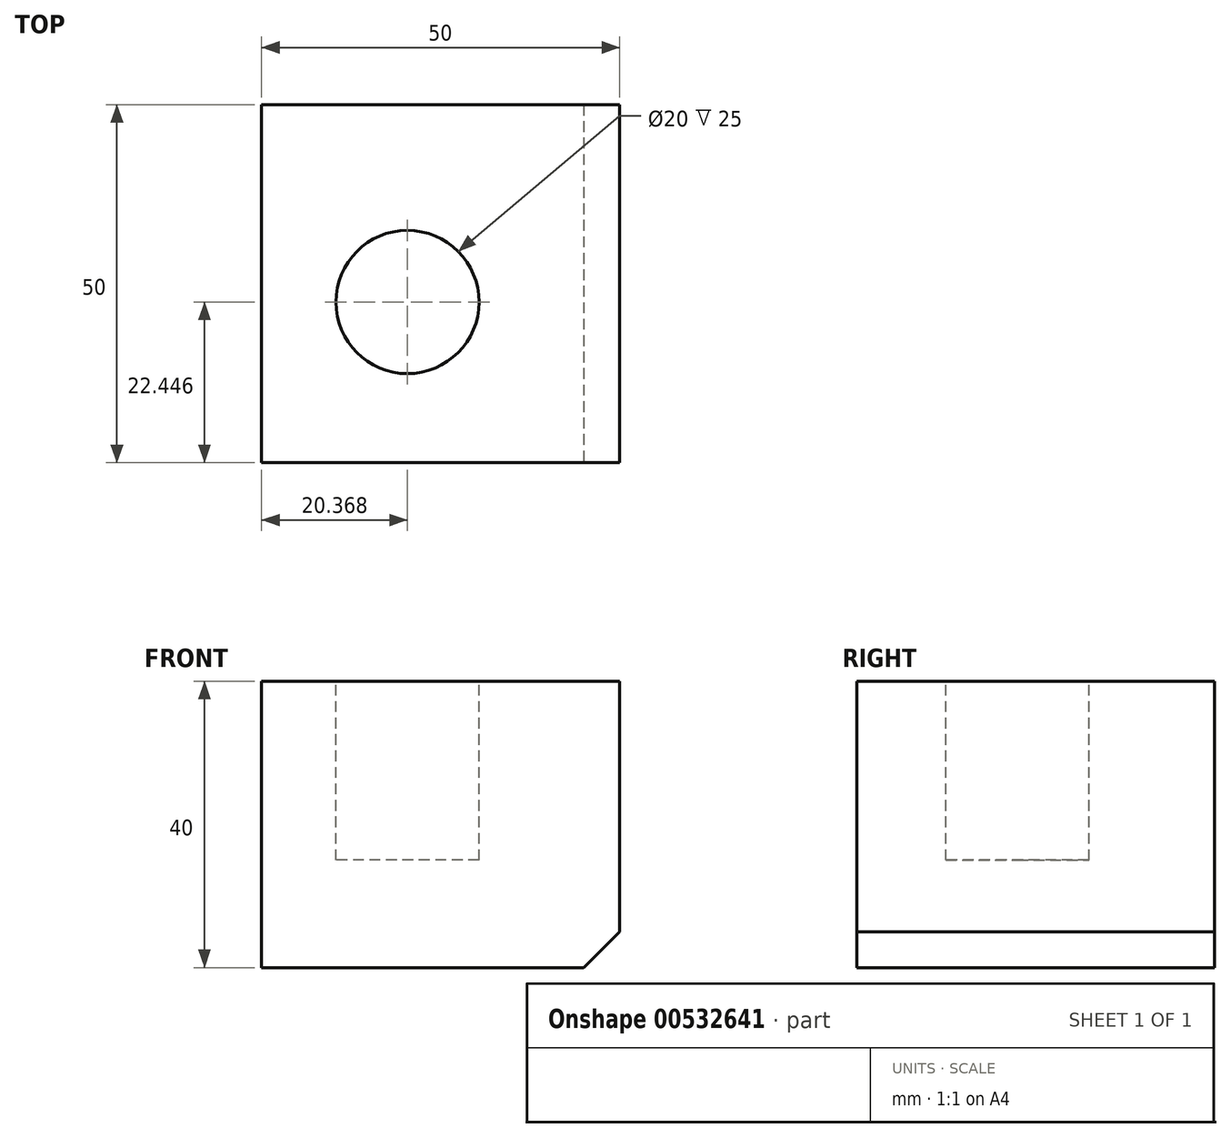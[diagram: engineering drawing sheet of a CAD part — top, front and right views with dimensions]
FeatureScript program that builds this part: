
annotation { "Feature Type Name" : "Feature", "Feature Type Description" : "" }
export const myFeature = defineFeature(function(context is Context, id is Id, definition is map)
    precondition{}
    {
        {
            var Q0;
            Q0=qCreatedBy(makeId("Front.planeOp"),FACE);
            var sketch = newSketch(context, id + "F0", { "sketchPlane" : qUnion([Q0])});
            skLineSegment(sketch, "E0.bottom", {"start": v(-34.47, 21.82) * mm, "end": v(15.53, 21.82) * mm});
            skLineSegment(sketch, "E0.top", {"start": v(-34.47, -18.18) * mm, "end": v(15.53, -18.18) * mm});
            skLineSegment(sketch, "E0.left", {"start": v(-34.47, 21.82) * mm, "end": v(-34.47, -18.18) * mm});
            skLineSegment(sketch, "E0.right", {"start": v(15.53, 21.82) * mm, "end": v(15.53, -18.18) * mm});
            skSolve(sketch);
        }
        {
            var Q0;
            Q0=makeQuery(id+"F0.imprint","IMPRINT",FACE,{"disambiguationData":[TD([[makeQuery(id+"F0.imprint","IMPRINT",EDGE,{"derivedFrom":sQuery(id+"F0.wireOp",EDGE,"E0.bottom")}),-1.0]])]});
            extrude(context, id + "F1", {"entities" : qUnion([Q0]), "depth" : 50 * mm, "offsetDistance" : 25.4 * mm});
        }
        {
            var Q0;
            Q0=makeQuery(id+"F1.opExtrude","SWEPT_FACE",FACE,{"disambiguationData":[OSD([sQuery(id+"F0.wireOp",EDGE,"E0.bottom")])]});
            var sketch = newSketch(context, id + "F2", { "sketchPlane" : qUnion([Q0])});
            skCircle(sketch, "E1", {"center": v(-14.1, -27.55) * mm, "radius": 10 * mm});
            skSolve(sketch);
        }
        {
            var Q0;
            Q0=makeQuery(id+"F2.imprint","IMPRINT",FACE,{"disambiguationData":[TD([[makeQuery(id+"F2.imprint","IMPRINT",EDGE,{"derivedFrom":sQuery(id+"F2.wireOp",EDGE,"E1")}),1.0]])]});
            extrude(context, id + "F3", {"entities" : qUnion([Q0]), "operationType" : NewBodyOperationType.REMOVE, "oppositeDirection" : true, "depth" : 25 * mm, "offsetDistance" : 25 * mm});
        }
        {
            var Q0;
            Q0=makeQuery(id+"F1.opExtrude","SWEPT_EDGE",EDGE,{"disambiguationData":[OSD([sQuery(id+"F0.wireOp",EDGE,"E0.top"),sQuery(id+"F0.wireOp",EDGE,"E0.right")])]});
            chamfer(context, id + "F4", {"entities" : qUnion([Q0]), "width" : 5 * mm, "tangentPropagation" : true});
        }
    });
